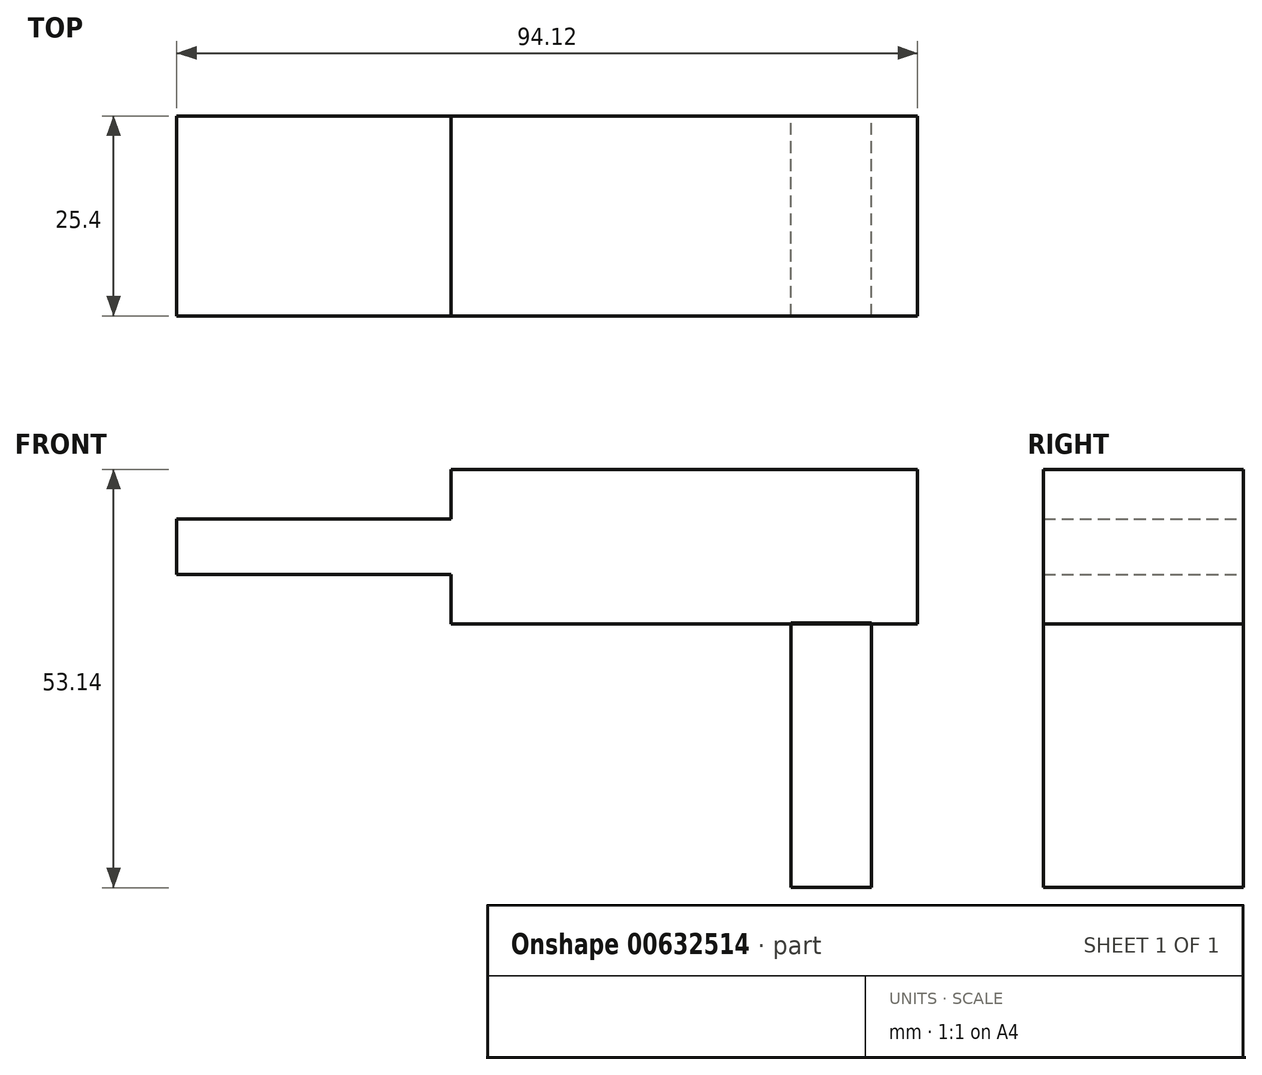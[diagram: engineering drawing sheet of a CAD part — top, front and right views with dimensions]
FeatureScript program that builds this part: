
annotation { "Feature Type Name" : "Feature", "Feature Type Description" : "" }
export const myFeature = defineFeature(function(context is Context, id is Id, definition is map)
    precondition{}
    {
        {
            var Q0;
            Q0=qCreatedBy(makeId("Front.planeOp"),FACE);
            var sketch = newSketch(context, id + "F0", { "sketchPlane" : qUnion([Q0])});
            skLineSegment(sketch, "E0.bottom", {"start": v(-29.65, 9.83) * mm, "end": v(29.65, 9.83) * mm});
            skLineSegment(sketch, "E0.top", {"start": v(-29.65, -9.83) * mm, "end": v(29.65, -9.83) * mm});
            skLineSegment(sketch, "E0.left", {"start": v(-29.65, 9.83) * mm, "end": v(-29.65, -9.83) * mm});
            skLineSegment(sketch, "E0.right", {"start": v(29.65, 9.83) * mm, "end": v(29.65, -9.83) * mm});
            skPoint(sketch, "E0.middle", {"position": v(0, 0) * mm});
            skLineSegment(sketch, "E1.bottom", {"start": v(-29.65, 3.53) * mm, "end": v(-64.47, 3.53) * mm});
            skLineSegment(sketch, "E1.top", {"start": v(-29.65, -3.53) * mm, "end": v(-64.47, -3.53) * mm});
            skLineSegment(sketch, "E1.left", {"start": v(-29.65, 3.53) * mm, "end": v(-29.65, -3.53) * mm});
            skLineSegment(sketch, "E1.right", {"start": v(-64.47, 3.53) * mm, "end": v(-64.47, -3.53) * mm});
            skPoint(sketch, "E1.middle", {"position": v(-47.06, 0) * mm});
            skPoint(sketch, "E1.middle.positionSnap0", {"position": v(-29.65, 0) * mm});
            skPoint(sketch, "E1.centerSnap0", {"position": v(-29.65, 0) * mm});
            skSolve(sketch);
        }
        {
            var Q0;
            Q0=qCreatedBy(makeId("Front.planeOp"),FACE);
            var sketch = newSketch(context, id + "F1", { "sketchPlane" : qUnion([Q0])});
            skLineSegment(sketch, "E2.bottom", {"start": v(13.59, -9.68) * mm, "end": v(23.8, -9.68) * mm});
            skLineSegment(sketch, "E2.top", {"start": v(13.59, -43.3) * mm, "end": v(23.8, -43.3) * mm});
            skLineSegment(sketch, "E2.left", {"start": v(13.59, -9.68) * mm, "end": v(13.59, -43.3) * mm});
            skLineSegment(sketch, "E2.right", {"start": v(23.8, -9.68) * mm, "end": v(23.8, -43.3) * mm});
            skSolve(sketch);
        }
        {
            var Q0;
            Q0=makeQuery(id+"F0.imprint","IMPRINT",FACE,{"disambiguationData":[TD([[makeQuery(id+"F0.imprint","IMPRINT",EDGE,{"derivedFrom":sQuery(id+"F0.wireOp",EDGE,"E1.bottom")}),1.0]])]});
            var Q1;
            {var subQ3=sQuery(id+"F0.wireOp",EDGE,"E0.bottom");Q1=makeQuery(id+"F0.imprint","IMPRINT",FACE,{"disambiguationData":[TD([[makeQuery(id+"F0.imprint","IMPRINT",EDGE,{"derivedFrom":subQ3}),-1.0]])]});}
            var Q2;
            Q2=makeQuery(id+"F1.imprint","IMPRINT",FACE,{"disambiguationData":[TD([[makeQuery(id+"F1.imprint","IMPRINT",EDGE,{"derivedFrom":sQuery(id+"F1.wireOp",EDGE,"E2.bottom")}),-1.0]])]});
            extrude(context, id + "F2", {"entities" : qUnion([Q0, Q1, Q2]), "depth" : 25.4 * mm, "offsetDistance" : 25.4 * mm});
        }
    });
